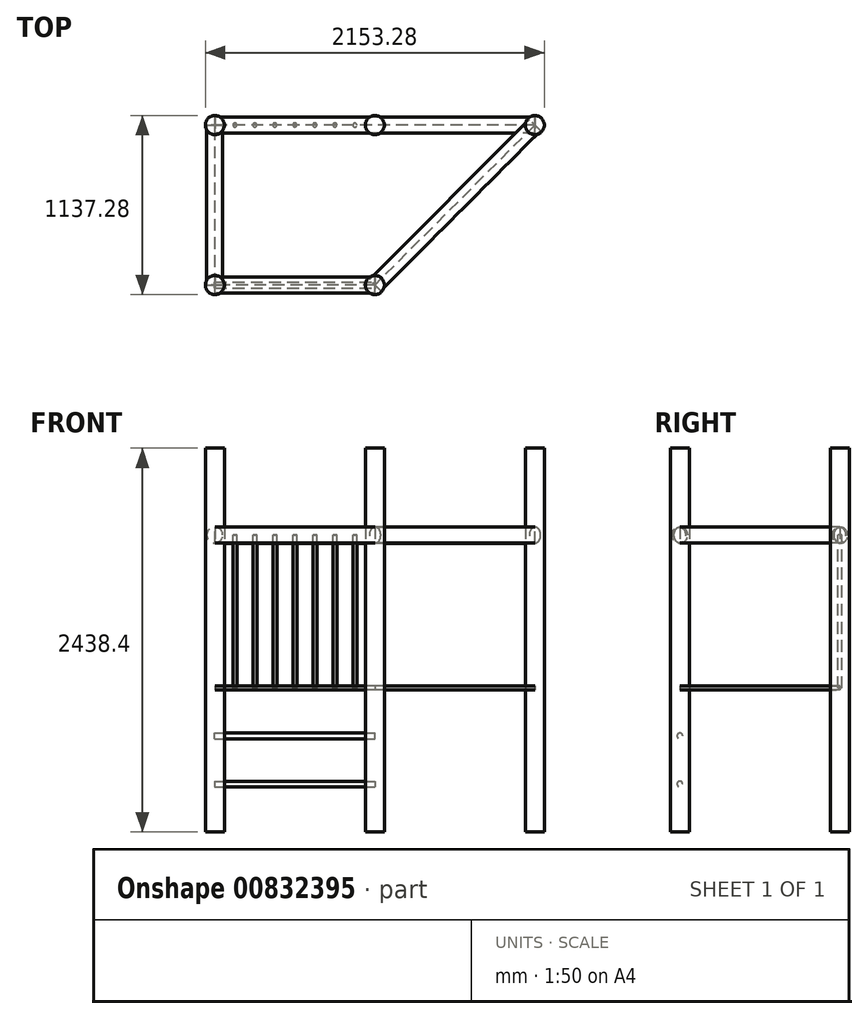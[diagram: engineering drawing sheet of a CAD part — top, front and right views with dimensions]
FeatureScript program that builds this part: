
annotation { "Feature Type Name" : "Feature", "Feature Type Description" : "" }
export const myFeature = defineFeature(function(context is Context, id is Id, definition is map)
    precondition{}
    {
        {
            var Q0;
            Q0=qCreatedBy(makeId("Top.planeOp"),FACE);
            var sketch = newSketch(context, id + "F0", { "sketchPlane" : qUnion([Q0])});
            skLineSegment(sketch, "E0.bottom", {"start": v(508, -508) * mm, "end": v(-508, -508) * mm});
            skLineSegment(sketch, "E0.top", {"start": v(508, 508) * mm, "end": v(-508, 508) * mm});
            skLineSegment(sketch, "E0.left", {"start": v(508, -508) * mm, "end": v(508, 508) * mm});
            skLineSegment(sketch, "E0.right", {"start": v(-508, -508) * mm, "end": v(-508, 508) * mm});
            skPoint(sketch, "E0.middle", {"position": v(0, 0) * mm});
            skPoint(sketch, "E1", {"position": v(-508, 508) * mm});
            skPoint(sketch, "E2", {"position": v(508, 508) * mm});
            skPoint(sketch, "E3", {"position": v(508, -508) * mm});
            skPoint(sketch, "E4", {"position": v(-508, -508) * mm});
            skLineSegment(sketch, "E5", {"start": v(508, 508) * mm, "end": v(1524, 508) * mm});
            skLineSegment(sketch, "E6", {"start": v(1524, 508) * mm, "end": v(508, -508) * mm});
            skSolve(sketch);
        }
        {
            var Q0;
            {var subQ10=sQuery(id+"F0.wireOp",EDGE,"OfH0pMX1-Unux-kOMp-M3el-kwdeYhqtyJaw");var subQ13=sQuery(id+"F0.wireOp",EDGE,"E0.bottom");var subQ14=makeQuery(id+"F0.imprint","INTERSECT",VERTEX,{"derivedFrom":[subQ13,subQ10]});Q0=makeQuery(id+"F0.imprint","IMPRINT",FACE,{"disambiguationData":[TD([[makeQuery(id+"F0.imprint","IMPRINT",EDGE,{"disambiguationData":[TD([[subQ14,-1.0]])],"derivedFrom":subQ13}),-1.0]])]});}
            var Q1;
            {var subQ3=sQuery(id+"F0.wireOp",EDGE,"OfH0pMX1-Unux-kOMp-M3el-kwdeYhqtyJaw");var subQ5=sQuery(id+"F0.wireOp",EDGE,"E0.left");var subQ6=makeQuery(id+"F0.imprint","INTERSECT",VERTEX,{"derivedFrom":[subQ5,subQ3]});Q1=makeQuery(id+"F0.imprint","IMPRINT",FACE,{"disambiguationData":[TD([[makeQuery(id+"F0.imprint","IMPRINT",EDGE,{"disambiguationData":[TD([[subQ6,-1.0]])],"derivedFrom":subQ5}),-1.0]])]});}
            extrude(context, id + "F1", {"entities" : qUnion([Q0, Q1]), "depth" : 12.7 * mm, "offsetDistance" : 25.4 * mm, "hasSecondDirection" : true, "secondDirectionOppositeDirection" : true, "secondDirectionDepth" : 12.7 * mm});
        }
        {
            var Q0;
            Q0=qCreatedBy(makeId("Top.planeOp"),FACE);
            var sketch = newSketch(context, id + "F2", { "sketchPlane" : qUnion([Q0])});
            skPoint(sketch, "E7", {"position": v(508, -508) * mm});
            skPoint(sketch, "E8", {"position": v(-508, -508) * mm});
            skPoint(sketch, "E9", {"position": v(-508, 508) * mm});
            skPoint(sketch, "E10", {"position": v(508, 508) * mm});
            skPoint(sketch, "E11", {"position": v(1524, 508) * mm});
            skCircle(sketch, "E12", {"center": v(-508, 508) * mm, "radius": 60.64 * mm});
            skCircle(sketch, "E13", {"center": v(508, 508) * mm, "radius": 60.64 * mm});
            skCircle(sketch, "E14", {"center": v(1524, 508) * mm, "radius": 60.64 * mm});
            skCircle(sketch, "E15", {"center": v(508, -508) * mm, "radius": 60.64 * mm});
            skCircle(sketch, "E16", {"center": v(-508, -508) * mm, "radius": 60.64 * mm});
            skSolve(sketch);
        }
        {
            var Q0;
            Q0 = qSketchRegion(id + "F2", true);
            extrude(context, id + "F3", {"entities" : qUnion([Q0]), "depth" : 1524 * mm, "offsetDistance" : 25.4 * mm, "hasSecondDirection" : true, "secondDirectionOppositeDirection" : true, "secondDirectionDepth" : 914.4 * mm});
        }
        {
            var Q0;
            Q0=sQuery(id+"F0.wireOp",VERTEX,"E4");
            var Q1;
            Q1=sQuery(id+"F0.wireOp",EDGE,"E0.right");
            cPlane(context, id + "F4", {"entities" : qUnion([Q0, Q1]), "cplaneType" : CPlaneType.LINE_POINT, "offset" : 25.4 * mm, "width" : 152.4 * mm, "height" : 152.4 * mm});
        }
        {
            var Q0;
            Q0=qCreatedBy(id+"F4.planeOp",FACE);
            var sketch = newSketch(context, id + "F5", { "sketchPlane" : qUnion([Q0])});
            skLineSegment(sketch, "E17", {"start": v(509.02, -304.8) * mm, "end": v(-509.05, -304.8) * mm});
            skLineSegment(sketch, "E18", {"start": v(-509.05, -609.6) * mm, "end": v(509.02, -609.6) * mm});
            skLineSegment(sketch, "E19", {"start": v(-507.72, 0) * mm, "end": v(-507.72, 971.55) * mm, "construction": true});
            skLineSegment(sketch, "E20", {"start": v(-507.72, 971.55) * mm, "end": v(508.28, 971.55) * mm, "construction": true});
            skLineSegment(sketch, "E21", {"start": v(508.28, 971.55) * mm, "end": v(508.28, 0) * mm, "construction": true});
            skLineSegment(sketch, "E22", {"start": v(-507.72, 971.55) * mm, "end": v(508.28, 971.55) * mm});
            skSolve(sketch);
        }
        {
            var Q0;
            Q0=sQuery(id+"F5.wireOp",VERTEX,"E17.start");
            var Q1;
            Q1=sQuery(id+"F5.wireOp",EDGE,"E17");
            cPlane(context, id + "F6", {"entities" : qUnion([Q0, Q1]), "cplaneType" : CPlaneType.LINE_POINT, "offset" : 25.4 * mm, "width" : 152.4 * mm, "height" : 152.4 * mm});
        }
        {
            var Q0;
            Q0=qCreatedBy(id+"F6.planeOp",FACE);
            var sketch = newSketch(context, id + "F7", { "sketchPlane" : qUnion([Q0])});
            skCircle(sketch, "E23", {"center": v(-507.54, -304.34) * mm, "radius": 18.16 * mm});
            skSolve(sketch);
        }
        {
            var Q0;
            Q0=sQuery(id+"F5.wireOp",VERTEX,"E18.end");
            var Q1;
            Q1=sQuery(id+"F5.wireOp",EDGE,"E18");
            cPlane(context, id + "F8", {"entities" : qUnion([Q0, Q1]), "cplaneType" : CPlaneType.LINE_POINT, "offset" : 25.4 * mm, "width" : 152.4 * mm, "height" : 152.4 * mm});
        }
        {
            var Q0;
            Q0=qCreatedBy(id+"F8.planeOp",FACE);
            var sketch = newSketch(context, id + "F9", { "sketchPlane" : qUnion([Q0])});
            skCircle(sketch, "E24", {"center": v(507.9, -609.84) * mm, "radius": 18.16 * mm});
            skSolve(sketch);
        }
        {
            var Q0;
            Q0 = qSketchRegion(id + "F7", true);
            var Q1;
            Q1=sQuery(id+"F5.wireOp",EDGE,"E17");
            sweep(context, id + "F10", {"profiles" : qUnion([Q0]), "path" : qUnion([Q1])});
        }
        {
            var Q0;
            Q0 = qSketchRegion(id + "F9", true);
            var Q1;
            Q1=sQuery(id+"F5.wireOp",EDGE,"E18");
            sweep(context, id + "F11", {"profiles" : qUnion([Q0]), "path" : qUnion([Q1])});
        }
        {
            var Q0;
            Q0=sQuery(id+"F5.wireOp",VERTEX,"E19.end");
            var Q1;
            Q1=sQuery(id+"F5.wireOp",EDGE,"E22");
            cPlane(context, id + "F12", {"entities" : qUnion([Q0, Q1]), "cplaneType" : CPlaneType.LINE_POINT, "offset" : 25.4 * mm, "width" : 152.4 * mm, "height" : 152.4 * mm});
        }
        {
            var Q0;
            Q0=qCreatedBy(id+"F12.planeOp",FACE);
            var sketch = newSketch(context, id + "F13", { "sketchPlane" : qUnion([Q0])});
            skCircle(sketch, "E25", {"center": v(508.14, 971.55) * mm, "radius": 50.8 * mm});
            skSolve(sketch);
        }
        {
            var Q0;
            Q0 = qSketchRegion(id + "F13", true);
            var Q1;
            Q1=sQuery(id+"F13.wireOp",EDGE,"E25");
            var Q2;
            Q2=sQuery(id+"F5.wireOp",EDGE,"E22");
            var Q3;
            Q3 = qConstructionFilter(qBodyType(qCreatedBy(id + "F15" ,EDGE), BodyType.WIRE), ConstructionObject.NO);
            sweep(context, id + "F14", {"profiles" : qUnion([Q0]), "surfaceProfiles" : qUnion([Q1]), "path" : qUnion([Q2, Q3])});
        }
        {
            var Q0;
            Q0=qCreatedBy(makeId("Top.planeOp"),FACE);
            var sketch = newSketch(context, id + "F15", { "sketchPlane" : qUnion([Q0])});
            skLineSegment(sketch, "E26", {"start": v(1017.12, 0) * mm, "end": v(508, 508) * mm, "construction": true});
            skSolve(sketch);
        }
        {
            var Q0;
            Q0=sQuery(id+"F15.wireOp",EDGE,"E26");
            var Q1;
            Q1=sQuery(id+"F15.wireOp",VERTEX,"E26.start");
            cPlane(context, id + "F16", {"entities" : qUnion([Q0, Q1]), "cplaneType" : CPlaneType.LINE_POINT, "offset" : 25.4 * mm, "width" : 152.4 * mm, "height" : 152.4 * mm});
        }
        {
            var Q0;
            Q0=qCreatedBy(id+"F16.planeOp",FACE);
            var sketch = newSketch(context, id + "F17", { "sketchPlane" : qUnion([Q0])});
            skLineSegment(sketch, "E27", {"start": v(0, 0) * mm, "end": v(-1436.84, 0) * mm, "construction": true});
            skLineSegment(sketch, "E28", {"start": v(-1436.84, 0) * mm, "end": v(-1436.84, 971.55) * mm, "construction": true});
            skLineSegment(sketch, "E29", {"start": v(-1436.84, 971.55) * mm, "end": v(0, 971.55) * mm, "construction": true});
            skLineSegment(sketch, "E30", {"start": v(0, 971.55) * mm, "end": v(0, 0) * mm, "construction": true});
            skLineSegment(sketch, "E31", {"start": v(-1436.84, 971.55) * mm, "end": v(0, 971.55) * mm});
            skSolve(sketch);
        }
        {
            var Q0;
            Q0=sQuery(id+"F17.wireOp",EDGE,"E31");
            var Q1;
            Q1=sQuery(id+"F17.wireOp",VERTEX,"E28.end");
            cPlane(context, id + "F18", {"entities" : qUnion([Q0, Q1]), "cplaneType" : CPlaneType.LINE_POINT, "offset" : 25.4 * mm, "width" : 152.4 * mm, "height" : 152.4 * mm});
        }
        {
            var Q0;
            Q0=qCreatedBy(id+"F18.planeOp",FACE);
            var sketch = newSketch(context, id + "F19", { "sketchPlane" : qUnion([Q0])});
            skCircle(sketch, "E32", {"center": v(720.33, 971.58) * mm, "radius": 50.8 * mm});
            skSolve(sketch);
        }
        {
            var Q0;
            Q0 = qSketchRegion(id + "F19", true);
            var Q1;
            Q1=sQuery(id+"F17.wireOp",EDGE,"E31");
            sweep(context, id + "F20", {"profiles" : qUnion([Q0]), "path" : qUnion([Q1])});
        }
        {
            var Q0;
            Q0=sQuery(id+"F5.wireOp",VERTEX,"E20.end");
            var Q1;
            Q1=sQuery(id+"F5.wireOp",EDGE,"E22");
            cPlane(context, id + "F21", {"entities" : qUnion([Q0, Q1]), "cplaneType" : CPlaneType.LINE_POINT, "offset" : 25.4 * mm, "width" : 152.4 * mm, "height" : 152.4 * mm});
        }
        {
            var Q0;
            Q0=qCreatedBy(id+"F21.planeOp",FACE);
            var sketch = newSketch(context, id + "F22", { "sketchPlane" : qUnion([Q0])});
            skLineSegment(sketch, "E33", {"start": v(507.49, 970.48) * mm, "end": v(-508.51, 970.48) * mm, "construction": true});
            skLineSegment(sketch, "E34", {"start": v(507.49, 970.48) * mm, "end": v(-508.51, 970.48) * mm});
            skSolve(sketch);
        }
        {
            var Q0;
            Q0=sQuery(id+"F22.wireOp",VERTEX,"E33.end");
            var Q1;
            Q1=sQuery(id+"F22.wireOp",EDGE,"E34");
            cPlane(context, id + "F23", {"entities" : qUnion([Q0, Q1]), "cplaneType" : CPlaneType.LINE_POINT, "offset" : 25.4 * mm, "width" : 152.4 * mm, "height" : 152.4 * mm});
        }
        {
            var Q0;
            Q0=qCreatedBy(id+"F23.planeOp",FACE);
            var sketch = newSketch(context, id + "F24", { "sketchPlane" : qUnion([Q0])});
            skCircle(sketch, "E35", {"center": v(508.63, 972.27) * mm, "radius": 50.8 * mm});
            skSolve(sketch);
        }
        {
            var Q0;
            Q0 = qSketchRegion(id + "F24", true);
            var Q1;
            Q1=sQuery(id+"F22.wireOp",EDGE,"E34");
            sweep(context, id + "F25", {"profiles" : qUnion([Q0]), "path" : qUnion([Q1])});
        }
        {
            var Q0;
            Q0=qCreatedBy(id+"F23.planeOp",FACE);
            var sketch = newSketch(context, id + "F26", { "sketchPlane" : qUnion([Q0])});
            skLineSegment(sketch, "E36", {"start": v(508, 971.55) * mm, "end": v(-508, 971.55) * mm});
            skLineSegment(sketch, "E37", {"start": v(-508, 971.55) * mm, "end": v(-1524, 971.55) * mm});
            skLineSegment(sketch, "E38", {"start": v(508, 971.55) * mm, "end": v(381, 971.55) * mm, "construction": true});
            skLineSegment(sketch, "E39", {"start": v(381, 971.55) * mm, "end": v(254, 971.55) * mm, "construction": true});
            skLineSegment(sketch, "E40", {"start": v(254, 971.55) * mm, "end": v(127, 971.55) * mm, "construction": true});
            skLineSegment(sketch, "E41", {"start": v(127, 971.55) * mm, "end": v(0, 971.55) * mm, "construction": true});
            skLineSegment(sketch, "E42", {"start": v(0, 971.55) * mm, "end": v(-127, 971.55) * mm, "construction": true});
            skLineSegment(sketch, "E43", {"start": v(-127, 971.55) * mm, "end": v(-254, 971.55) * mm, "construction": true});
            skLineSegment(sketch, "E44", {"start": v(-254, 971.55) * mm, "end": v(-381, 971.55) * mm, "construction": true});
            skLineSegment(sketch, "E45", {"start": v(-381, 971.55) * mm, "end": v(-508, 971.55) * mm, "construction": true});
            skLineSegment(sketch, "E46", {"start": v(381, 971.55) * mm, "end": v(381, 0) * mm});
            skLineSegment(sketch, "E47", {"start": v(254, 971.55) * mm, "end": v(254, 0) * mm});
            skLineSegment(sketch, "E48", {"start": v(127, 971.55) * mm, "end": v(127, 0) * mm});
            skLineSegment(sketch, "E49", {"start": v(0, 971.55) * mm, "end": v(0, 0) * mm});
            skLineSegment(sketch, "E50", {"start": v(-127, 971.55) * mm, "end": v(-127, 0) * mm});
            skLineSegment(sketch, "E51", {"start": v(-254, 971.55) * mm, "end": v(-254, 0) * mm});
            skLineSegment(sketch, "E52", {"start": v(-381, 971.55) * mm, "end": v(-381, 0) * mm});
            skSolve(sketch);
        }
        {
            var Q0;
            Q0=sQuery(id+"F26.wireOp",VERTEX,"E37.end");
            var Q1;
            Q1=sQuery(id+"F26.wireOp",EDGE,"E37");
            cPlane(context, id + "F27", {"entities" : qUnion([Q0, Q1]), "cplaneType" : CPlaneType.LINE_POINT, "offset" : 25.4 * mm, "width" : 152.4 * mm, "height" : 152.4 * mm});
        }
        {
            var Q0;
            Q0=qCreatedBy(id+"F27.planeOp",FACE);
            var sketch = newSketch(context, id + "F28", { "sketchPlane" : qUnion([Q0])});
            skCircle(sketch, "E53", {"center": v(508.49, 970.38) * mm, "radius": 50.8 * mm});
            skSolve(sketch);
        }
        {
            var Q0;
            Q0 = qSketchRegion(id + "F28", true);
            var Q1;
            Q1=sQuery(id+"F26.wireOp",EDGE,"E37");
            var Q2;
            Q2=sQuery(id+"F26.wireOp",EDGE,"E36");
            sweep(context, id + "F29", {"profiles" : qUnion([Q0]), "path" : qUnion([Q1, Q2])});
        }
        {
            var Q0;
            Q0=sQuery(id+"F26.wireOp",VERTEX,"E52.end");
            var Q1;
            Q1=sQuery(id+"F26.wireOp",EDGE,"E52");
            cPlane(context, id + "F30", {"entities" : qUnion([Q0, Q1]), "cplaneType" : CPlaneType.LINE_POINT, "offset" : 25.4 * mm, "width" : 152.4 * mm, "height" : 152.4 * mm});
        }
        {
            var Q0;
            Q0=qCreatedBy(id+"F30.planeOp",FACE);
            var sketch = newSketch(context, id + "F31", { "sketchPlane" : qUnion([Q0])});
            skCircle(sketch, "E54", {"center": v(381.2, -507.67) * mm, "radius": 12.7 * mm});
            skCircle(sketch, "E55", {"center": v(254.48, -509.13) * mm, "radius": 12.7 * mm});
            skCircle(sketch, "E56", {"center": v(126.93, -508.52) * mm, "radius": 12.7 * mm});
            skCircle(sketch, "E57", {"center": v(0, -508.94) * mm, "radius": 12.7 * mm});
            skCircle(sketch, "E58", {"center": v(-127.04, -508.53) * mm, "radius": 12.7 * mm});
            skCircle(sketch, "E59", {"center": v(-254.31, -508.15) * mm, "radius": 12.7 * mm});
            skCircle(sketch, "E60", {"center": v(-380.9, -508.38) * mm, "radius": 12.7 * mm});
            skSolve(sketch);
        }
        {
            var Q0;
            Q0 = qSketchRegion(id + "F31", true);
            var Q1;
            Q1=sQuery(id+"F31.wireOp",EDGE,"E54");
            var Q2;
            Q2=sQuery(id+"F26.wireOp",EDGE,"E52");
            sweep(context, id + "F32", {"profiles" : qUnion([Q0]), "surfaceProfiles" : qUnion([Q1]), "path" : qUnion([Q2])});
        }
        {
            var Q0;
            Q0 = qSketchRegion(id + "F31", true);
            var Q1;
            Q1=sQuery(id+"F26.wireOp",EDGE,"E51");
            sweep(context, id + "F33", {"profiles" : qUnion([Q0]), "path" : qUnion([Q1])});
        }
    });
